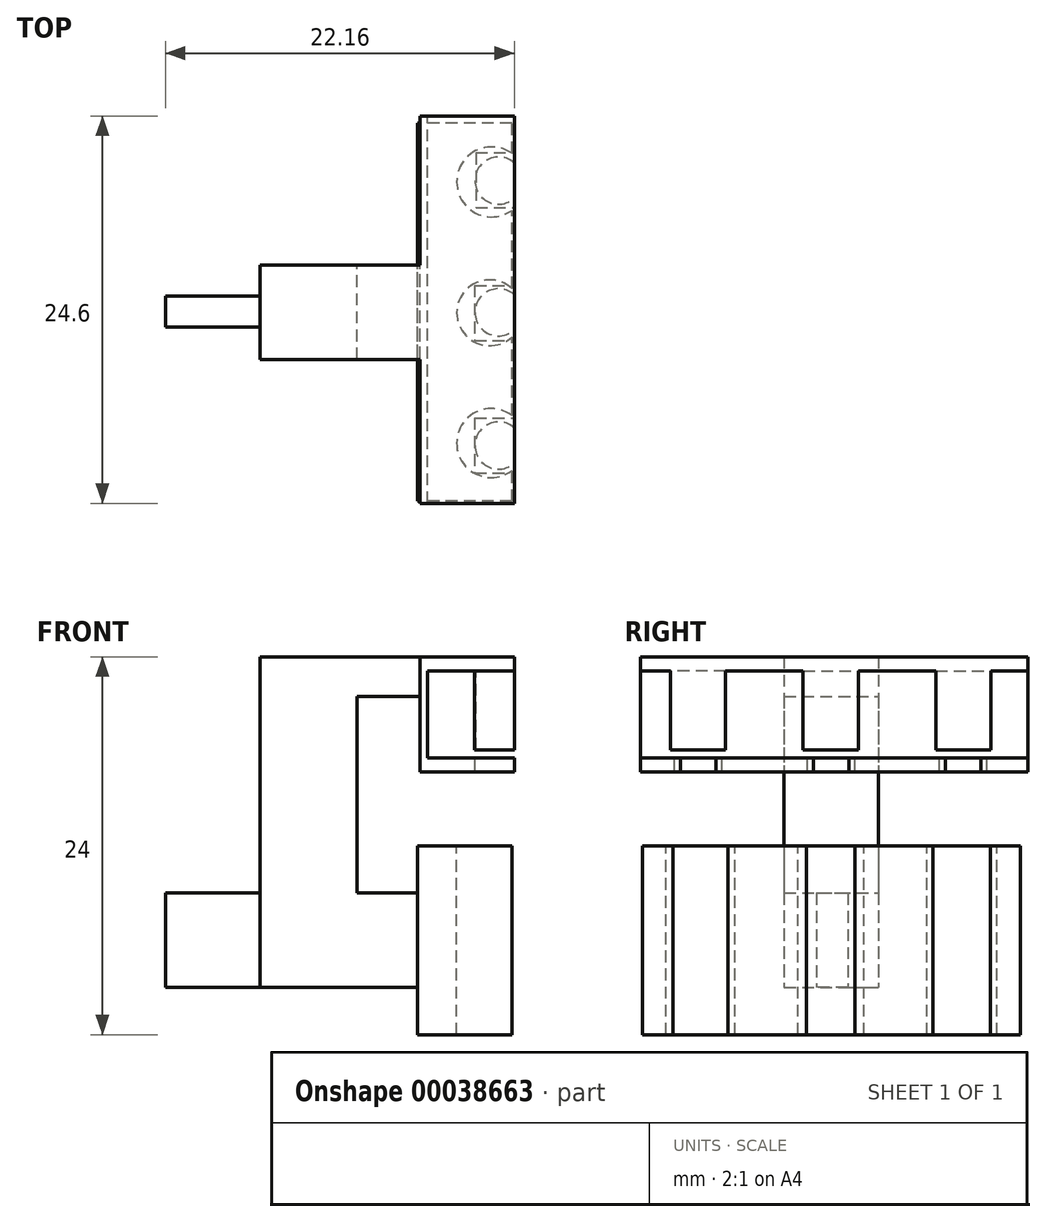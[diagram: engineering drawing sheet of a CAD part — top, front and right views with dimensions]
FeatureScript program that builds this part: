
annotation { "Feature Type Name" : "Feature", "Feature Type Description" : "" }
export const myFeature = defineFeature(function(context is Context, id is Id, definition is map)
    precondition{}
    {
        {
            var Q0;
            Q0=qCreatedBy(makeId("Top.planeOp"),FACE);
            var sketch = newSketch(context, id + "F0", { "sketchPlane" : qUnion([Q0])});
            skLineSegment(sketch, "E0.bottom", {"start": v(-35.05, 0) * mm, "end": v(-29.05, 0) * mm});
            skLineSegment(sketch, "E0.top", {"start": v(-35.05, -2) * mm, "end": v(-29.05, -2) * mm});
            skLineSegment(sketch, "E0.left", {"start": v(-35.05, 0) * mm, "end": v(-35.05, -2) * mm});
            skLineSegment(sketch, "E0.right", {"start": v(-29.05, 0) * mm, "end": v(-29.05, -2) * mm});
            skSolve(sketch);
        }
        {
            var Q0;
            Q0 = qSketchRegion(id + "F0", true);
            extrude(context, id + "F1", {"entities" : qUnion([Q0]), "depth" : 6 * mm});
        }
        {
            var Q0;
            Q0=makeQuery(id+"F1.opExtrude","SWEPT_FACE",FACE,{"disambiguationData":[OSD([sQuery(id+"F0.wireOp",EDGE,"E0.right")])]});
            var sketch = newSketch(context, id + "F2", { "sketchPlane" : qUnion([Q0])});
            skLineSegment(sketch, "E1.bottom", {"start": v(-4.04, 6) * mm, "end": v(1.96, 6) * mm});
            skLineSegment(sketch, "E1.top", {"start": v(-4.04, 0) * mm, "end": v(1.96, 0) * mm});
            skLineSegment(sketch, "E1.left", {"start": v(-4.04, 6) * mm, "end": v(-4.04, 0) * mm});
            skLineSegment(sketch, "E1.right", {"start": v(1.96, 6) * mm, "end": v(1.96, 0) * mm});
            skSolve(sketch);
        }
        {
            var Q0;
            Q0 = qSketchRegion(id + "F2", true);
            extrude(context, id + "F3", {"entities" : qUnion([Q0]), "operationType" : NewBodyOperationType.ADD, "depth" : 10 * mm});
        }
        {
            var Q0;
            Q0=makeQuery(id+"F3.opExtrude","CAP_FACE",FACE,{"disambiguationData":[OSD([sQuery(id+"F2.wireOp",EDGE,"E1.bottom"),sQuery(id+"F2.wireOp",EDGE,"E1.top"),sQuery(id+"F2.wireOp",EDGE,"E1.left"),sQuery(id+"F2.wireOp",EDGE,"E1.right")])],"isStart":false});
            var sketch = newSketch(context, id + "F4", { "sketchPlane" : qUnion([Q0])});
            skLineSegment(sketch, "E2.bottom", {"start": v(-13.04, 9) * mm, "end": v(10.96, 9) * mm});
            skLineSegment(sketch, "E2.top", {"start": v(-13.04, -3) * mm, "end": v(10.96, -3) * mm});
            skLineSegment(sketch, "E2.left", {"start": v(-13.04, 9) * mm, "end": v(-13.04, -3) * mm});
            skLineSegment(sketch, "E2.right", {"start": v(10.96, 9) * mm, "end": v(10.96, -3) * mm});
            skSolve(sketch);
        }
        {
            var Q0;
            Q0 = qSketchRegion(id + "F4", true);
            extrude(context, id + "F5", {"entities" : qUnion([Q0]), "operationType" : NewBodyOperationType.ADD, "depth" : 6 * mm});
        }
        {
            var Q0;
            Q0=makeQuery(id+"F5.opExtrude","SWEPT_FACE",FACE,{"disambiguationData":[OSD([sQuery(id+"F4.wireOp",EDGE,"E2.bottom")])]});
            var sketch = newSketch(context, id + "F6", { "sketchPlane" : qUnion([Q0])});
            skCircle(sketch, "E3", {"center": v(-14.36, -9.35) * mm, "radius": 2.19 * mm});
            skCircle(sketch, "E4", {"center": v(-14.46, -1.08) * mm, "radius": 2.09 * mm});
            skCircle(sketch, "E5", {"center": v(-14.33, 7.23) * mm, "radius": 2.22 * mm});
            skSolve(sketch);
        }
        {
            var Q0;
            {var subQ0=makeQuery(id+"F5.opExtrude","CAP_EDGE",EDGE,{"disambiguationData":[OSD([sQuery(id+"F4.wireOp",EDGE,"E2.bottom")])],"isStart":false});var subQ1=sQuery(id+"F6.wireOp",EDGE,"E3");var subQ3=makeQuery(id+"F6.imprint","INTERSECT",VERTEX,{"disambiguationData":[OD(0.0)],"derivedFrom":[subQ0,subQ1]});Q0=makeQuery(id+"F6.imprint","IMPRINT",FACE,{"disambiguationData":[TD([[makeQuery(id+"F6.imprint","IMPRINT",EDGE,{"disambiguationData":[TD([[subQ3,1.0]])],"derivedFrom":subQ1}),1.0]])]});}
            var Q1;
            {var subQ0=makeQuery(id+"F5.opExtrude","CAP_EDGE",EDGE,{"disambiguationData":[OSD([sQuery(id+"F4.wireOp",EDGE,"E2.bottom")])],"isStart":false});var subQ1=sQuery(id+"F6.wireOp",EDGE,"E4");var subQ3=makeQuery(id+"F6.imprint","INTERSECT",VERTEX,{"disambiguationData":[OD(0.0)],"derivedFrom":[subQ0,subQ1]});Q1=makeQuery(id+"F6.imprint","IMPRINT",FACE,{"disambiguationData":[TD([[makeQuery(id+"F6.imprint","IMPRINT",EDGE,{"disambiguationData":[TD([[subQ3,1.0]])],"derivedFrom":subQ1}),1.0]])]});}
            var Q2;
            {var subQ0=makeQuery(id+"F5.opExtrude","CAP_EDGE",EDGE,{"disambiguationData":[OSD([sQuery(id+"F4.wireOp",EDGE,"E2.bottom")])],"isStart":false});var subQ1=sQuery(id+"F6.wireOp",EDGE,"E5");var subQ3=makeQuery(id+"F6.imprint","INTERSECT",VERTEX,{"disambiguationData":[OD(0.0)],"derivedFrom":[subQ0,subQ1]});Q2=makeQuery(id+"F6.imprint","IMPRINT",FACE,{"disambiguationData":[TD([[makeQuery(id+"F6.imprint","IMPRINT",EDGE,{"disambiguationData":[TD([[subQ3,-1.0]])],"derivedFrom":subQ1}),1.0]])]});}
            extrude(context, id + "F7", {"entities" : qUnion([Q0, Q1, Q2]), "operationType" : NewBodyOperationType.REMOVE, "endBound" : BoundingType.THROUGH_ALL, "oppositeDirection" : true, "depth" : 25 * mm});
        }
        {
            var Q0;
            Q0=makeQuery(id+"F3.boolean.opBoolean","MERGE",FACE,{"derivedFrom":[makeQuery(id+"F1.opExtrude","CAP_FACE",FACE,{"disambiguationData":[OSD([sQuery(id+"F0.wireOp",EDGE,"E0.bottom"),sQuery(id+"F0.wireOp",EDGE,"E0.top"),sQuery(id+"F0.wireOp",EDGE,"E0.left"),sQuery(id+"F0.wireOp",EDGE,"E0.right")])],"isStart":false}),makeQuery(id+"F3.opExtrude","SWEPT_FACE",FACE,{"disambiguationData":[OSD([sQuery(id+"F2.wireOp",EDGE,"E1.bottom")])]})]});
            var sketch = newSketch(context, id + "F8", { "sketchPlane" : qUnion([Q0])});
            skLineSegment(sketch, "E6.bottom", {"start": v(-29.05, -4.04) * mm, "end": v(-22.89, -4.04) * mm});
            skLineSegment(sketch, "E6.top", {"start": v(-29.05, 1.96) * mm, "end": v(-22.89, 1.96) * mm});
            skLineSegment(sketch, "E6.left", {"start": v(-29.05, -4.04) * mm, "end": v(-29.05, 1.96) * mm});
            skLineSegment(sketch, "E6.right", {"start": v(-22.89, -4.04) * mm, "end": v(-22.89, 1.96) * mm});
            skSolve(sketch);
        }
        {
            var Q0;
            Q0 = qSketchRegion(id + "F8", true);
            extrude(context, id + "F9", {"entities" : qUnion([Q0]), "operationType" : NewBodyOperationType.ADD, "depth" : 15 * mm});
        }
        {
            var Q0;
            Q0=makeQuery(id+"F9.opExtrude","SWEPT_FACE",FACE,{"disambiguationData":[OSD([sQuery(id+"F8.wireOp",EDGE,"E6.right")])]});
            var sketch = newSketch(context, id + "F10", { "sketchPlane" : qUnion([Q0])});
            skLineSegment(sketch, "E7.bottom", {"start": v(-4.04, 21) * mm, "end": v(1.96, 21) * mm});
            skLineSegment(sketch, "E7.top", {"start": v(-4.04, 18.48) * mm, "end": v(1.96, 18.48) * mm});
            skLineSegment(sketch, "E7.left", {"start": v(-4.04, 21) * mm, "end": v(-4.04, 18.48) * mm});
            skLineSegment(sketch, "E7.right", {"start": v(1.96, 21) * mm, "end": v(1.96, 18.48) * mm});
            skSolve(sketch);
        }
        {
            var Q0;
            Q0 = qSketchRegion(id + "F10", true);
            extrude(context, id + "F11", {"entities" : qUnion([Q0]), "operationType" : NewBodyOperationType.ADD, "depth" : 4 * mm});
        }
        {
            var Q0;
            Q0=makeQuery(id+"F11.opExtrude","CAP_FACE",FACE,{"disambiguationData":[OSD([sQuery(id+"F10.wireOp",EDGE,"E7.bottom"),sQuery(id+"F10.wireOp",EDGE,"E7.top"),sQuery(id+"F10.wireOp",EDGE,"E7.left"),sQuery(id+"F10.wireOp",EDGE,"E7.right")])],"isStart":false});
            var sketch = newSketch(context, id + "F12", { "sketchPlane" : qUnion([Q0])});
            skLineSegment(sketch, "E8.bottom", {"start": v(-13.18, 21) * mm, "end": v(11.42, 21) * mm});
            skLineSegment(sketch, "E8.top", {"start": v(-13.18, 13.7) * mm, "end": v(11.42, 13.7) * mm});
            skLineSegment(sketch, "E8.left", {"start": v(-13.18, 21) * mm, "end": v(-13.18, 13.7) * mm});
            skLineSegment(sketch, "E8.right", {"start": v(11.42, 21) * mm, "end": v(11.42, 13.7) * mm});
            skSolve(sketch);
        }
        {
            var Q0;
            Q0 = qSketchRegion(id + "F12", true);
            extrude(context, id + "F13", {"entities" : qUnion([Q0]), "operationType" : NewBodyOperationType.ADD, "depth" : 6 * mm});
        }
        {
            var Q0;
            Q0=makeQuery(id+"F13.opExtrude","SWEPT_FACE",FACE,{"disambiguationData":[OSD([sQuery(id+"F12.wireOp",EDGE,"E8.right")])]});
            var sketch = newSketch(context, id + "F14", { "sketchPlane" : qUnion([Q0])});
            skLineSegment(sketch, "E9.bottom", {"start": v(12.89, 20.1) * mm, "end": v(18.39, 20.1) * mm});
            skLineSegment(sketch, "E9.top", {"start": v(12.89, 14.57) * mm, "end": v(18.39, 14.57) * mm});
            skLineSegment(sketch, "E9.left", {"start": v(12.89, 20.1) * mm, "end": v(12.89, 14.57) * mm});
            skLineSegment(sketch, "E9.right", {"start": v(18.39, 20.1) * mm, "end": v(18.39, 14.57) * mm});
            skSolve(sketch);
        }
        {
            var Q0;
            Q0 = qSketchRegion(id + "F14", true);
            extrude(context, id + "F15", {"entities" : qUnion([Q0]), "operationType" : NewBodyOperationType.REMOVE, "endBound" : BoundingType.THROUGH_ALL, "oppositeDirection" : true, "depth" : 25 * mm});
        }
        {
            var Q0;
            Q0=makeQuery(id+"F15.boolean.opBoolean","COPY",FACE,{"derivedFrom":makeQuery(id+"F15.opExtrude","SWEPT_FACE",FACE,{"disambiguationData":[OSD([sQuery(id+"F14.wireOp",EDGE,"E9.top")])]})});
            var sketch = newSketch(context, id + "F16", { "sketchPlane" : qUnion([Q0])});
            skCircle(sketch, "E10", {"center": v(-13.89, -9.5) * mm, "radius": 1.5 * mm});
            skCircle(sketch, "E11", {"center": v(-13.89, -1.05) * mm, "radius": 1.5 * mm});
            skCircle(sketch, "E12", {"center": v(-13.89, 7.32) * mm, "radius": 1.5 * mm});
            skSolve(sketch);
        }
        {
            var Q0;
            Q0 = qSketchRegion(id + "F16", true);
            extrude(context, id + "F17", {"entities" : qUnion([Q0]), "operationType" : NewBodyOperationType.REMOVE, "oppositeDirection" : true, "depth" : 1 * mm});
        }
        {
            var Q0;
            Q0=makeQuery(id+"F15.boolean.opBoolean","COPY",FACE,{"derivedFrom":makeQuery(id+"F15.opExtrude","SWEPT_FACE",FACE,{"disambiguationData":[OSD([sQuery(id+"F14.wireOp",EDGE,"E9.bottom")])]})});
            var sketch = newSketch(context, id + "F18", { "sketchPlane" : qUnion([Q0])});
            skLineSegment(sketch, "E13.bottom", {"start": v(-15.34, -9.09) * mm, "end": v(-12.89, -9.09) * mm});
            skLineSegment(sketch, "E13.top", {"start": v(-15.34, -5.59) * mm, "end": v(-12.89, -5.59) * mm});
            skLineSegment(sketch, "E13.left", {"start": v(-15.34, -9.09) * mm, "end": v(-15.34, -5.59) * mm});
            skLineSegment(sketch, "E13.right", {"start": v(-12.89, -9.09) * mm, "end": v(-12.89, -5.59) * mm});
            skLineSegment(sketch, "E14.bottom", {"start": v(-15.41, -0.67) * mm, "end": v(-12.89, -0.67) * mm});
            skLineSegment(sketch, "E14.top", {"start": v(-15.41, 2.83) * mm, "end": v(-12.89, 2.83) * mm});
            skLineSegment(sketch, "E14.left", {"start": v(-15.41, -0.67) * mm, "end": v(-15.41, 2.83) * mm});
            skLineSegment(sketch, "E14.right", {"start": v(-12.89, -0.67) * mm, "end": v(-12.89, 2.83) * mm});
            skLineSegment(sketch, "E15.bottom", {"start": v(-15.41, 7.76) * mm, "end": v(-12.89, 7.76) * mm});
            skLineSegment(sketch, "E15.top", {"start": v(-15.41, 11.26) * mm, "end": v(-12.89, 11.26) * mm});
            skLineSegment(sketch, "E15.left", {"start": v(-15.41, 7.76) * mm, "end": v(-15.41, 11.26) * mm});
            skLineSegment(sketch, "E15.right", {"start": v(-12.89, 7.76) * mm, "end": v(-12.89, 11.26) * mm});
            skSolve(sketch);
        }
        {
            var Q0;
            Q0 = qSketchRegion(id + "F18", true);
            extrude(context, id + "F19", {"entities" : qUnion([Q0]), "operationType" : NewBodyOperationType.ADD, "depth" : 5 * mm});
        }
    });
